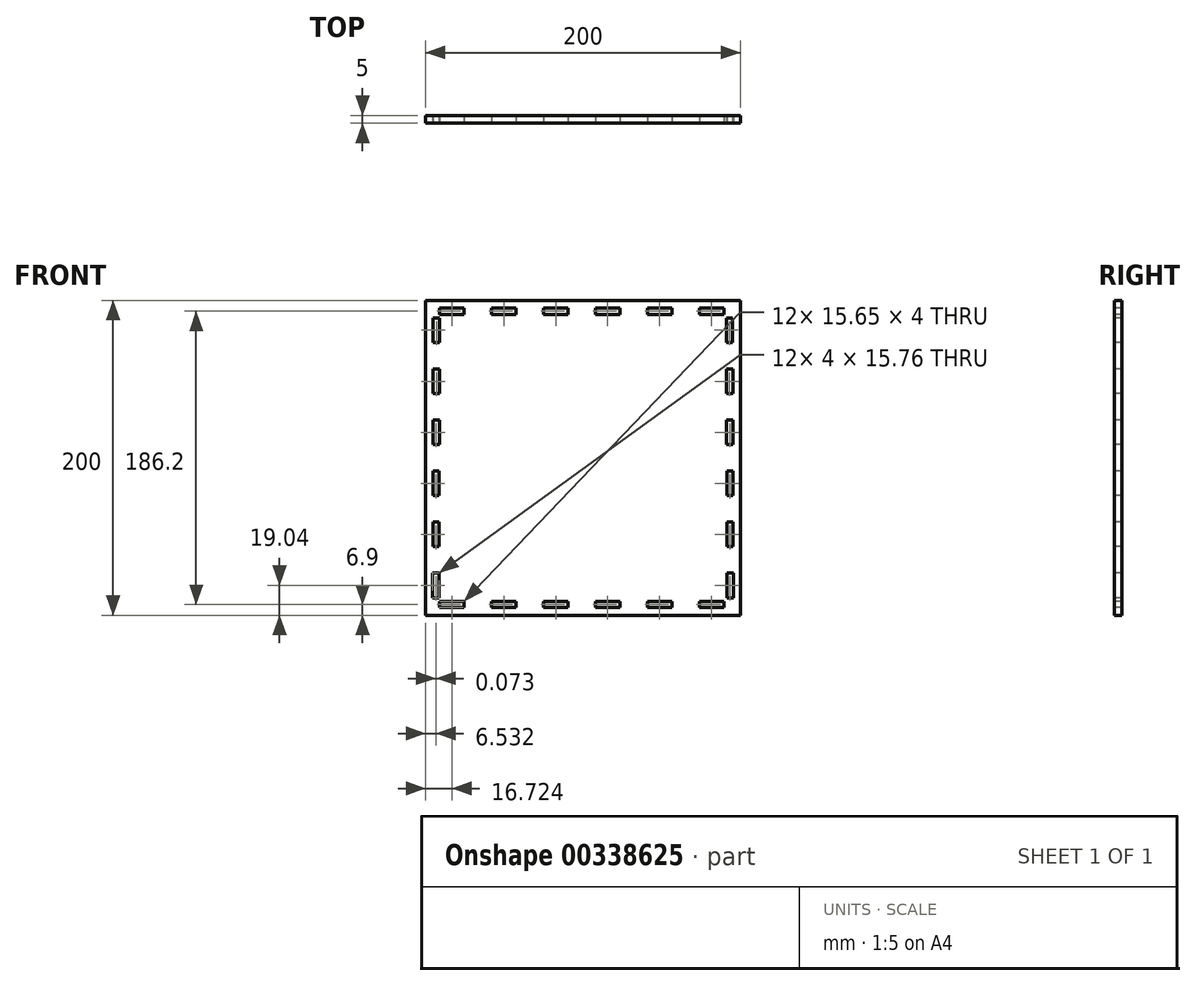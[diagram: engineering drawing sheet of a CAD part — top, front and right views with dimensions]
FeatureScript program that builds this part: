
annotation { "Feature Type Name" : "Feature", "Feature Type Description" : "" }
export const myFeature = defineFeature(function(context is Context, id is Id, definition is map)
    precondition{}
    {
        {
            var Q0;
            Q0=qCreatedBy(makeId("Front.planeOp"),FACE);
            var sketch = newSketch(context, id + "F0", { "sketchPlane" : qUnion([Q0])});
            skLineSegment(sketch, "E0.bottom", {"start": v(-100, 100) * mm, "end": v(100, 100) * mm});
            skLineSegment(sketch, "E0.top", {"start": v(-100, -100) * mm, "end": v(100, -100) * mm});
            skLineSegment(sketch, "E0.left", {"start": v(-100, 100) * mm, "end": v(-100, -100) * mm});
            skLineSegment(sketch, "E0.right", {"start": v(100, 100) * mm, "end": v(100, -100) * mm});
            skPoint(sketch, "E0.middle", {"position": v(0, 0) * mm});
            skSolve(sketch);
        }
        {
            var Q0;
            Q0 = qSketchRegion(id + "F0", true);
            extrude(context, id + "F1", {"entities" : qUnion([Q0]), "depth" : 5 * mm, "offsetDistance" : 25 * mm});
        }
        {
            var Q0;
            Q0=makeQuery(id+"F1.opExtrude","CAP_FACE",FACE,{"disambiguationData":[OSD([sQuery(id+"F0.wireOp",EDGE,"E0.bottom"),sQuery(id+"F0.wireOp",EDGE,"E0.top"),sQuery(id+"F0.wireOp",EDGE,"E0.left"),sQuery(id+"F0.wireOp",EDGE,"E0.right")])],"isStart":false});
            var sketch = newSketch(context, id + "F2", { "sketchPlane" : qUnion([Q0])});
            skLineSegment(sketch, "E1.bottom", {"start": v(-91.1, 95.1) * mm, "end": v(-75.45, 95.1) * mm});
            skLineSegment(sketch, "E1.top", {"start": v(-91.1, 91.1) * mm, "end": v(-75.45, 91.1) * mm});
            skLineSegment(sketch, "E1.left", {"start": v(-91.1, 95.1) * mm, "end": v(-91.1, 91.1) * mm});
            skLineSegment(sketch, "E1.right", {"start": v(-75.45, 95.1) * mm, "end": v(-75.45, 91.1) * mm});
            skLineSegment(sketch, "E2.1.0.0", {"start": v(-42.45, 95.1) * mm, "end": v(-42.45, 91.1) * mm});
            skLineSegment(sketch, "E2.1.0.1", {"start": v(-58.1, 95.1) * mm, "end": v(-42.45, 95.1) * mm});
            skLineSegment(sketch, "E2.1.0.2", {"start": v(-58.1, 95.1) * mm, "end": v(-58.1, 91.1) * mm});
            skLineSegment(sketch, "E2.1.0.3", {"start": v(-58.1, 91.1) * mm, "end": v(-42.45, 91.1) * mm});
            skLineSegment(sketch, "E2.2.0.0", {"start": v(-9.45, 95.1) * mm, "end": v(-9.45, 91.1) * mm});
            skLineSegment(sketch, "E2.2.0.1", {"start": v(-25.1, 95.1) * mm, "end": v(-9.45, 95.1) * mm});
            skLineSegment(sketch, "E2.2.0.2", {"start": v(-25.1, 95.1) * mm, "end": v(-25.1, 91.1) * mm});
            skLineSegment(sketch, "E2.2.0.3", {"start": v(-25.1, 91.1) * mm, "end": v(-9.45, 91.1) * mm});
            skLineSegment(sketch, "E2.3.0.0", {"start": v(23.55, 95.1) * mm, "end": v(23.55, 91.1) * mm});
            skLineSegment(sketch, "E2.3.0.1", {"start": v(7.9, 95.1) * mm, "end": v(23.55, 95.1) * mm});
            skLineSegment(sketch, "E2.3.0.2", {"start": v(7.9, 95.1) * mm, "end": v(7.9, 91.1) * mm});
            skLineSegment(sketch, "E2.3.0.3", {"start": v(7.9, 91.1) * mm, "end": v(23.55, 91.1) * mm});
            skLineSegment(sketch, "E2.4.0.0", {"start": v(56.55, 95.1) * mm, "end": v(56.55, 91.1) * mm});
            skLineSegment(sketch, "E2.4.0.1", {"start": v(40.9, 95.1) * mm, "end": v(56.55, 95.1) * mm});
            skLineSegment(sketch, "E2.4.0.2", {"start": v(40.9, 95.1) * mm, "end": v(40.9, 91.1) * mm});
            skLineSegment(sketch, "E2.4.0.3", {"start": v(40.9, 91.1) * mm, "end": v(56.55, 91.1) * mm});
            skLineSegment(sketch, "E2.5.0.0", {"start": v(89.55, 95.1) * mm, "end": v(89.55, 91.1) * mm});
            skLineSegment(sketch, "E2.5.0.1", {"start": v(73.9, 95.1) * mm, "end": v(89.55, 95.1) * mm});
            skLineSegment(sketch, "E2.5.0.2", {"start": v(73.9, 95.1) * mm, "end": v(73.9, 91.1) * mm});
            skLineSegment(sketch, "E2.5.0.3", {"start": v(73.9, 91.1) * mm, "end": v(89.55, 91.1) * mm});
            skLineSegment(sketch, "E2.direction1", {"start": v(-75.45, 91.1) * mm, "end": v(-42.45, 91.1) * mm, "construction": true});
            skLineSegment(sketch, "E3", {"start": v(-100, 0) * mm, "end": v(100, 0) * mm, "construction": true});
            skLineSegment(sketch, "E4", {"start": v(0, 100) * mm, "end": v(0, -100) * mm, "construction": true});
            skLineSegment(sketch, "E5.MirrorCS", {"start": v(-91.1, -95.1) * mm, "end": v(-91.1, -91.1) * mm});
            skLineSegment(sketch, "E6.MirrorCS", {"start": v(-91.1, -95.1) * mm, "end": v(-75.45, -95.1) * mm});
            skLineSegment(sketch, "E7.MirrorCS", {"start": v(-75.45, -95.1) * mm, "end": v(-75.45, -91.1) * mm});
            skLineSegment(sketch, "E8.MirrorCS", {"start": v(-91.1, -91.1) * mm, "end": v(-75.45, -91.1) * mm});
            skLineSegment(sketch, "E9.MirrorCS", {"start": v(-58.1, -95.1) * mm, "end": v(-42.45, -95.1) * mm});
            skLineSegment(sketch, "E10.MirrorCS", {"start": v(-58.1, -95.1) * mm, "end": v(-58.1, -91.1) * mm});
            skLineSegment(sketch, "E11.MirrorCS", {"start": v(-42.45, -95.1) * mm, "end": v(-42.45, -91.1) * mm});
            skLineSegment(sketch, "E12.MirrorCS", {"start": v(-58.1, -91.1) * mm, "end": v(-42.45, -91.1) * mm});
            skLineSegment(sketch, "E13.MirrorCS", {"start": v(-25.1, -95.1) * mm, "end": v(-25.1, -91.1) * mm});
            skLineSegment(sketch, "E14.MirrorCS", {"start": v(-25.1, -95.1) * mm, "end": v(-9.45, -95.1) * mm});
            skLineSegment(sketch, "E15.MirrorCS", {"start": v(-9.45, -95.1) * mm, "end": v(-9.45, -91.1) * mm});
            skLineSegment(sketch, "E16.MirrorCS", {"start": v(-25.1, -91.1) * mm, "end": v(-9.45, -91.1) * mm});
            skLineSegment(sketch, "E17.MirrorCS", {"start": v(7.9, -95.1) * mm, "end": v(7.9, -91.1) * mm});
            skLineSegment(sketch, "E18.MirrorCS", {"start": v(7.9, -95.1) * mm, "end": v(23.55, -95.1) * mm});
            skLineSegment(sketch, "E19.MirrorCS", {"start": v(23.55, -95.1) * mm, "end": v(23.55, -91.1) * mm});
            skLineSegment(sketch, "E20.MirrorCS", {"start": v(7.9, -91.1) * mm, "end": v(23.55, -91.1) * mm});
            skLineSegment(sketch, "E21.MirrorCS", {"start": v(40.9, -95.1) * mm, "end": v(56.55, -95.1) * mm});
            skLineSegment(sketch, "E22.MirrorCS", {"start": v(40.9, -95.1) * mm, "end": v(40.9, -91.1) * mm});
            skLineSegment(sketch, "E23.MirrorCS", {"start": v(56.55, -95.1) * mm, "end": v(56.55, -91.1) * mm});
            skLineSegment(sketch, "E24.MirrorCS", {"start": v(40.9, -91.1) * mm, "end": v(56.55, -91.1) * mm});
            skLineSegment(sketch, "E25.MirrorCS", {"start": v(73.9, -95.1) * mm, "end": v(73.9, -91.1) * mm});
            skLineSegment(sketch, "E26.MirrorCS", {"start": v(73.9, -95.1) * mm, "end": v(89.55, -95.1) * mm});
            skLineSegment(sketch, "E27.MirrorCS", {"start": v(89.55, -95.1) * mm, "end": v(89.55, -91.1) * mm});
            skLineSegment(sketch, "E28.MirrorCS", {"start": v(73.9, -91.1) * mm, "end": v(89.55, -91.1) * mm});
            skLineSegment(sketch, "E29.bottom", {"start": v(95.1, 88.92) * mm, "end": v(91.1, 88.92) * mm});
            skLineSegment(sketch, "E29.top", {"start": v(95.1, 73.16) * mm, "end": v(91.1, 73.16) * mm});
            skLineSegment(sketch, "E29.left", {"start": v(95.1, 88.92) * mm, "end": v(95.1, 73.16) * mm});
            skLineSegment(sketch, "E29.right", {"start": v(91.1, 88.92) * mm, "end": v(91.1, 73.16) * mm});
            skLineSegment(sketch, "E30.1.0.0", {"start": v(95.17, 56.52) * mm, "end": v(95.17, 40.76) * mm});
            skLineSegment(sketch, "E30.1.0.1", {"start": v(95.17, 56.52) * mm, "end": v(91.17, 56.52) * mm});
            skLineSegment(sketch, "E30.1.0.2", {"start": v(95.17, 40.76) * mm, "end": v(91.17, 40.76) * mm});
            skLineSegment(sketch, "E30.1.0.3", {"start": v(91.17, 56.52) * mm, "end": v(91.17, 40.76) * mm});
            skLineSegment(sketch, "E30.2.0.0", {"start": v(95.25, 24.12) * mm, "end": v(95.25, 8.36) * mm});
            skLineSegment(sketch, "E30.2.0.1", {"start": v(95.25, 24.12) * mm, "end": v(91.25, 24.12) * mm});
            skLineSegment(sketch, "E30.2.0.2", {"start": v(95.25, 8.36) * mm, "end": v(91.25, 8.36) * mm});
            skLineSegment(sketch, "E30.2.0.3", {"start": v(91.25, 24.12) * mm, "end": v(91.25, 8.36) * mm});
            skLineSegment(sketch, "E30.3.0.0", {"start": v(95.32, -8.28) * mm, "end": v(95.32, -24.04) * mm});
            skLineSegment(sketch, "E30.3.0.1", {"start": v(95.32, -8.28) * mm, "end": v(91.32, -8.28) * mm});
            skLineSegment(sketch, "E30.3.0.2", {"start": v(95.32, -24.04) * mm, "end": v(91.32, -24.04) * mm});
            skLineSegment(sketch, "E30.3.0.3", {"start": v(91.32, -8.28) * mm, "end": v(91.32, -24.04) * mm});
            skLineSegment(sketch, "E30.4.0.0", {"start": v(95.4, -40.68) * mm, "end": v(95.4, -56.44) * mm});
            skLineSegment(sketch, "E30.4.0.1", {"start": v(95.4, -40.68) * mm, "end": v(91.4, -40.68) * mm});
            skLineSegment(sketch, "E30.4.0.2", {"start": v(95.4, -56.44) * mm, "end": v(91.4, -56.44) * mm});
            skLineSegment(sketch, "E30.4.0.3", {"start": v(91.4, -40.68) * mm, "end": v(91.4, -56.44) * mm});
            skLineSegment(sketch, "E30.5.0.0", {"start": v(95.47, -73.08) * mm, "end": v(95.47, -88.84) * mm});
            skLineSegment(sketch, "E30.5.0.1", {"start": v(95.47, -73.08) * mm, "end": v(91.47, -73.08) * mm});
            skLineSegment(sketch, "E30.5.0.2", {"start": v(95.47, -88.84) * mm, "end": v(91.47, -88.84) * mm});
            skLineSegment(sketch, "E30.5.0.3", {"start": v(91.47, -73.08) * mm, "end": v(91.47, -88.84) * mm});
            skLineSegment(sketch, "E30.direction1", {"start": v(95.1, 73.16) * mm, "end": v(95.17, 40.76) * mm, "construction": true});
            skLineSegment(sketch, "E31.MirrorCS", {"start": v(-95.1, 88.92) * mm, "end": v(-91.1, 88.92) * mm});
            skLineSegment(sketch, "E32.MirrorCS", {"start": v(-95.1, 88.92) * mm, "end": v(-95.1, 73.16) * mm});
            skLineSegment(sketch, "E33.MirrorCS", {"start": v(-95.1, 73.16) * mm, "end": v(-91.1, 73.16) * mm});
            skLineSegment(sketch, "E34.MirrorCS", {"start": v(-91.1, 88.92) * mm, "end": v(-91.1, 73.16) * mm});
            skLineSegment(sketch, "E35.MirrorCS", {"start": v(-95.1, 73.16) * mm, "end": v(-95.17, 40.76) * mm, "construction": true});
            skLineSegment(sketch, "E36.MirrorCS", {"start": v(-95.17, 56.52) * mm, "end": v(-91.17, 56.52) * mm});
            skLineSegment(sketch, "E37.MirrorCS", {"start": v(-95.17, 40.76) * mm, "end": v(-91.17, 40.76) * mm});
            skLineSegment(sketch, "E38.MirrorCS", {"start": v(-91.17, 56.52) * mm, "end": v(-91.17, 40.76) * mm});
            skLineSegment(sketch, "E39.MirrorCS", {"start": v(-95.17, 56.52) * mm, "end": v(-95.17, 40.76) * mm});
            skLineSegment(sketch, "E40.MirrorCS", {"start": v(-95.25, 24.12) * mm, "end": v(-95.25, 8.36) * mm});
            skLineSegment(sketch, "E41.MirrorCS", {"start": v(-95.25, 24.12) * mm, "end": v(-91.25, 24.12) * mm});
            skLineSegment(sketch, "E42.MirrorCS", {"start": v(-95.25, 8.36) * mm, "end": v(-91.25, 8.36) * mm});
            skLineSegment(sketch, "E43.MirrorCS", {"start": v(-91.25, 24.12) * mm, "end": v(-91.25, 8.36) * mm});
            skLineSegment(sketch, "E44.MirrorCS", {"start": v(-95.32, -8.28) * mm, "end": v(-95.32, -24.04) * mm});
            skLineSegment(sketch, "E45.MirrorCS", {"start": v(-95.32, -8.28) * mm, "end": v(-91.32, -8.28) * mm});
            skLineSegment(sketch, "E46.MirrorCS", {"start": v(-91.32, -8.28) * mm, "end": v(-91.32, -24.04) * mm});
            skLineSegment(sketch, "E47.MirrorCS", {"start": v(-95.32, -24.04) * mm, "end": v(-91.32, -24.04) * mm});
            skLineSegment(sketch, "E48.MirrorCS", {"start": v(-95.4, -40.68) * mm, "end": v(-95.4, -56.44) * mm});
            skLineSegment(sketch, "E49.MirrorCS", {"start": v(-95.4, -40.68) * mm, "end": v(-91.4, -40.68) * mm});
            skLineSegment(sketch, "E50.MirrorCS", {"start": v(-95.4, -56.44) * mm, "end": v(-91.4, -56.44) * mm});
            skLineSegment(sketch, "E51.MirrorCS", {"start": v(-91.4, -40.68) * mm, "end": v(-91.4, -56.44) * mm});
            skLineSegment(sketch, "E52.MirrorCS", {"start": v(-95.47, -73.08) * mm, "end": v(-95.47, -88.84) * mm});
            skLineSegment(sketch, "E53.MirrorCS", {"start": v(-95.47, -73.08) * mm, "end": v(-91.47, -73.08) * mm});
            skLineSegment(sketch, "E54.MirrorCS", {"start": v(-95.47, -88.84) * mm, "end": v(-91.47, -88.84) * mm});
            skLineSegment(sketch, "E55.MirrorCS", {"start": v(-91.47, -73.08) * mm, "end": v(-91.47, -88.84) * mm});
            skSolve(sketch);
        }
        {
            var Q0;
            Q0 = qSketchRegion(id + "F2", true);
            extrude(context, id + "F3", {"entities" : qUnion([Q0]), "operationType" : NewBodyOperationType.REMOVE, "oppositeDirection" : true, "depth" : 25 * mm, "offsetDistance" : 25 * mm});
        }
    });
